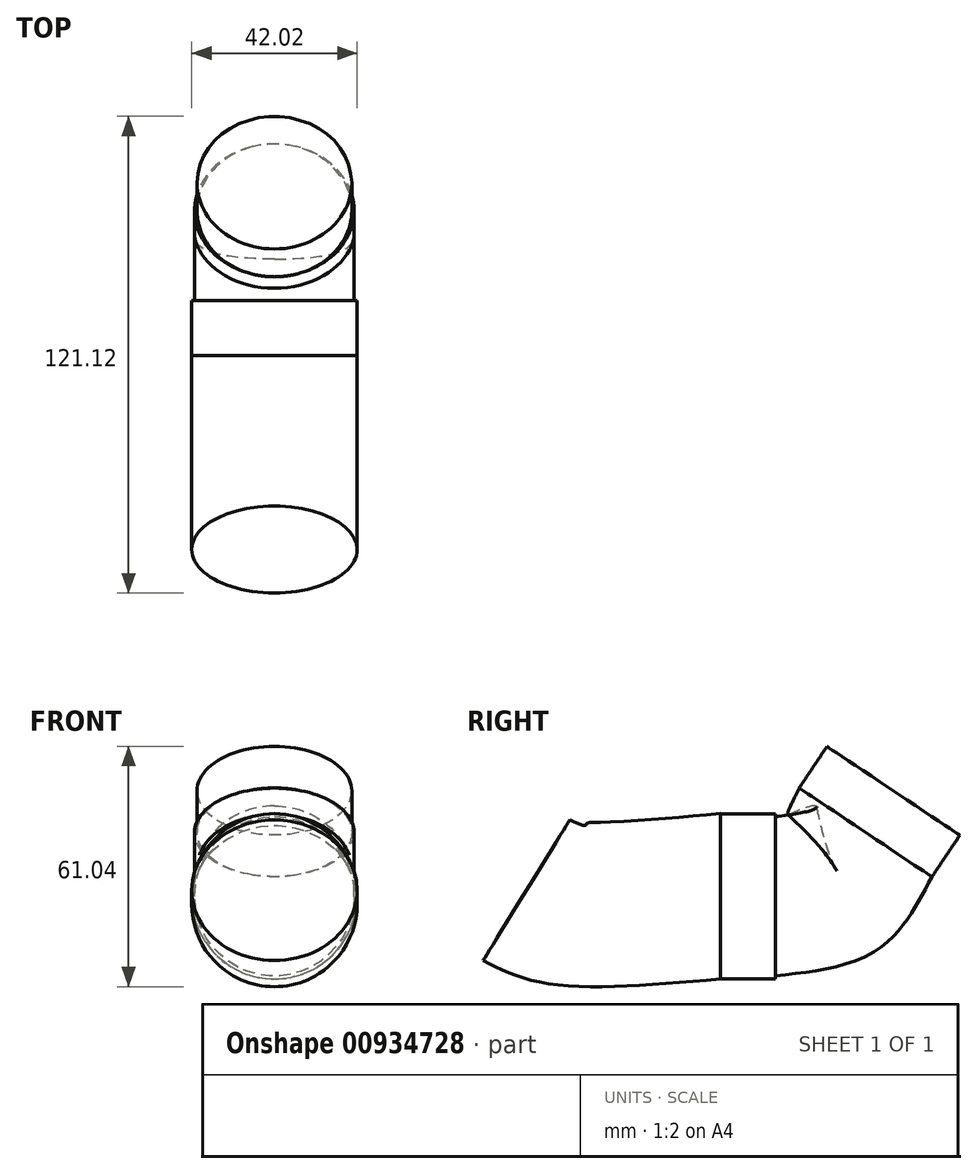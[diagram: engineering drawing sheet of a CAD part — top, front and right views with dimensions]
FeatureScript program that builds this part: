
annotation { "Feature Type Name" : "Feature", "Feature Type Description" : "" }
export const myFeature = defineFeature(function(context is Context, id is Id, definition is map)
    precondition{}
    {
        {
            var Q0;
            Q0=qCreatedBy(makeId("Front.planeOp"),FACE);
            var sketch = newSketch(context, id + "F0", { "sketchPlane" : qUnion([Q0])});
            skCircle(sketch, "E0", {"center": v(4.17, -5.61) * mm, "radius": 21.01 * mm});
            skSolve(sketch);
        }
        {
            var Q0;
            Q0=qCreatedBy(makeId("Right.planeOp"),FACE);
            var sketch = newSketch(context, id + "F1", { "sketchPlane" : qUnion([Q0])});
            skFitSpline(sketch, "E1", {"points": [v(0, -26.05) * mm, v(-43.9, -27.2) * mm, v(-60, -21.44) * mm], "startDerivative": vector(-80.33, -7.06) * mm, "endDerivative": vector(-36.29, 18.21) * mm});
            skSolve(sketch);
        }
        {
            var Q0;
            Q0=makeQuery(id+"F0.imprint","IMPRINT",FACE,{"disambiguationData":[TD([[makeQuery(id+"F0.imprint","IMPRINT",EDGE,{"derivedFrom":sQuery(id+"F0.wireOp",EDGE,"E0")}),1.0]])]});
            var Q1;
            Q1=sQuery(id+"F1.wireOp",EDGE,"E1");
            sweep(context, id + "F2", {"profiles" : qUnion([Q0]), "path" : qUnion([Q1])});
        }
        {
            var Q0;
            Q0=makeQuery(id+"F2.opSweep","CAP_FACE",FACE,{"disambiguationData":[OSD([sQuery(id+"F0.wireOp",EDGE,"E0"),sQuery(id+"F1.wireOp",VERTEX,"E1.start")])],"isStart":true});
            var sketch = newSketch(context, id + "F3", { "sketchPlane" : qUnion([Q0])});
            skCircle(sketch, "E2", {"center": v(-4.17, -5.61) * mm, "radius": 20.98 * mm});
            skSolve(sketch);
        }
        {
            var Q0;
            Q0 = qSketchRegion(id + "F3", true);
            extrude(context, id + "F4", {"entities" : qUnion([Q0]), "operationType" : NewBodyOperationType.ADD, "depth" : 13.97 * mm, "offsetDistance" : 25.4 * mm});
        }
        {
            var Q0;
            Q0=makeQuery(id+"F4.opExtrude","CAP_FACE",FACE,{"disambiguationData":[OSD([sQuery(id+"F3.wireOp",EDGE,"E2")])],"isStart":false});
            var sketch = newSketch(context, id + "F5", { "sketchPlane" : qUnion([Q0])});
            skCircle(sketch, "E3", {"center": v(-4.17, -5.61) * mm, "radius": 20.25 * mm});
            skSolve(sketch);
        }
        {
            var Q0;
            Q0=qCreatedBy(makeId("Right.planeOp"),FACE);
            var sketch = newSketch(context, id + "F6", { "sketchPlane" : qUnion([Q0])});
            skFitSpline(sketch, "E4", {"points": [v(13.71, -24.76) * mm, v(39.47, -18.1) * mm, v(52.77, 0) * mm], "startDerivative": vector(55.07, 6.25) * mm, "endDerivative": vector(22.6, 43.8) * mm});
            skSolve(sketch);
        }
        {
            var Q0;
            Q0=makeQuery(id+"F5.imprint","IMPRINT",FACE,{"disambiguationData":[TD([[makeQuery(id+"F5.imprint","IMPRINT",EDGE,{"derivedFrom":sQuery(id+"F5.wireOp",EDGE,"E3")}),1.0]])]});
            var Q1;
            Q1=sQuery(id+"F6.wireOp",EDGE,"E4");
            sweep(context, id + "F7", {"operationType" : NewBodyOperationType.ADD, "profiles" : qUnion([Q0]), "path" : qUnion([Q1])});
        }
        {
            var Q0;
            Q0=makeQuery(id+"F7.opSweep","CAP_FACE",FACE,{"disambiguationData":[OSD([sQuery(id+"F5.wireOp",EDGE,"E3"),sQuery(id+"F6.wireOp",VERTEX,"E4.end")])],"isStart":false});
            var sketch = newSketch(context, id + "F8", { "sketchPlane" : qUnion([Q0])});
            skEllipse(sketch, "E5", {"center": v(4.17, 24.75) * mm, "majorRadius": 20.3 * mm, "minorRadius": 19.68 * mm, "majorAxis": v(0, -1)});
            skSolve(sketch);
        }
        {
            var Q0;
            Q0 = qSketchRegion(id + "F8", true);
            extrude(context, id + "F9", {"entities" : qUnion([Q0]), "operationType" : NewBodyOperationType.ADD, "depth" : 12.7 * mm, "offsetDistance" : 25.4 * mm});
        }
    });
